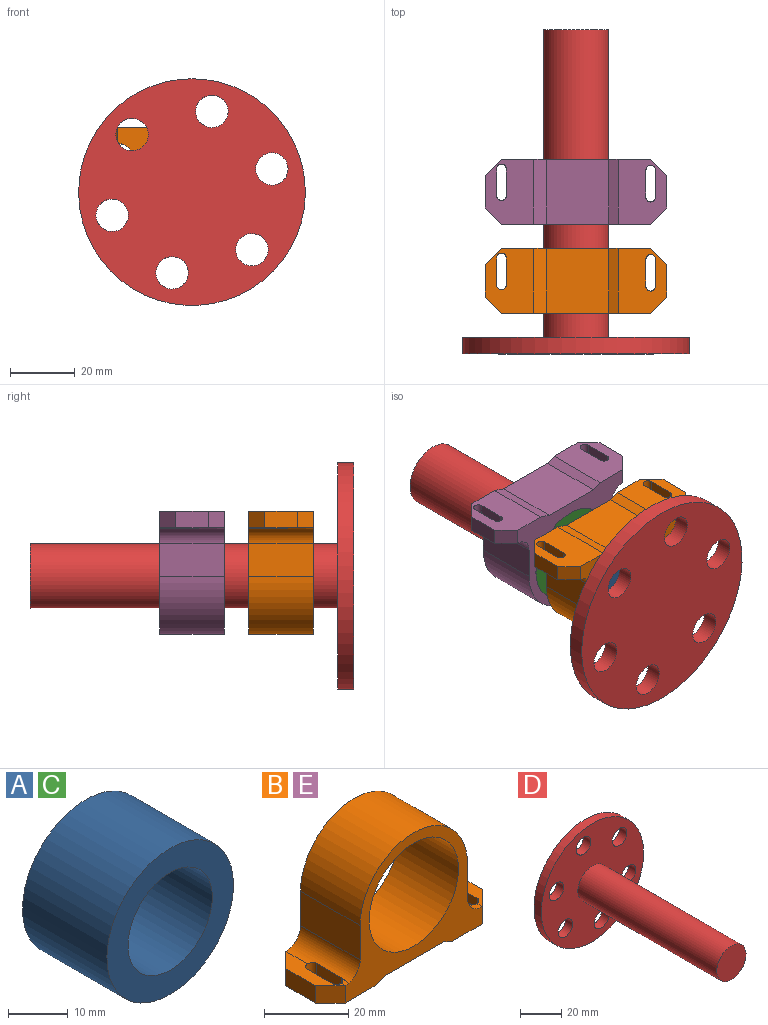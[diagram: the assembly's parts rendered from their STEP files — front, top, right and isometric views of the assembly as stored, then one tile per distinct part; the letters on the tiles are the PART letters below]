
ASSEMBLY  parts=5 mates=5
PART A: 4 faces, bbox 30x20x30 mm
  f0: cylinder r=10mm len=20mm, axis (0,1,0), area 1256.6mm2, adj f2,f3
  f1: cylinder r=15mm len=30mm, axis (0,1,0), area 1885mm2, adj f2,f3
  f2: plane 30x30mm, normal (0,-1,0), area 392.7mm2, adj f0,f1
  f3: plane 30x30mm, normal (0,1,0), area 392.7mm2, adj f0,f1
PART B: 33 faces, bbox 56x20x38 mm
  f0: plane 46x38mm, normal (0,-1,0), area 554.8mm2, adj f1,f2,f3,f6,f7,f8,f9,f10
  f1: plane 20x10.21mm, normal (1,0,0), area 202mm2, adj f0,f2,f13,f27,f28,f29,f30,f31
  f2: cylinder r=18mm len=36mm, axis (0,1,0), area 1131mm2, adj f0,f1,f3,f13
  f3: plane 20x10mm, normal (-1,0,0), area 200mm2, adj f0,f2,f13,f32
  f4: plane 20x5mm, normal (0,0,1), area 59.1mm2, adj f5,f20,f21,f22,f23,f24,f32
  f5: plane 10x5mm, normal (-1,0,0), area 50mm2, adj f4,f6,f23,f24
  f6: plane 20x15mm, normal (0,0,-1), area 243.1mm2, adj f0,f5,f7,f13,f19,f20,f21,f22
  f7: plane 20x3.8mm, normal (0.31,0,-0.95), area 80mm2, adj f0,f6,f8,f13
  f8: plane 20x19.25mm, normal (0,0,-1), area 385mm2, adj f0,f7,f9,f13
  f9: plane 20x2.95mm, normal (-0.39,0,-0.92), area 63.9mm2, adj f0,f8,f10,f13
  f10: plane 20x15mm, normal (0,0,-1), area 242.9mm2, adj f0,f9,f11,f13,f15,f16,f17,f18
  f11: plane 10x5mm, normal (1,0,0), area 50mm2, adj f10,f12,f25,f26
  f12: plane 20x5mm, normal (0,0,1), area 58.2mm2, adj f11,f15,f17,f18,f25,f26,f27,f31
  f13: plane 46x38mm, normal (0,1,0), area 554.8mm2, adj f1,f2,f3,f6,f7,f8,f9,f10
  f14: cylinder r=15mm len=30mm, axis (0,1,0), area 1885mm2, adj f0,f13
  f15: cylinder r=1.5mm len=5mm, axis (0,0,1), area 23.6mm2, adj f10,f12,f16,f18,f28
  f16: plane 8.33x5mm, normal (1,0,0), area 41.7mm2, adj f10,f15,f17,f29
  f17: cylinder r=1.5mm len=5mm, axis (0,0,1), area 23.6mm2, adj f10,f12,f16,f18,f30
  f18: plane 8.33x5mm, normal (-1,0,0), area 41.7mm2, adj f10,f12,f15,f17
  f19: plane 8.27x5.23mm, normal (-1,0,0), area 43.2mm2, adj f6,f20,f22,f32
  f20: cylinder r=1.5mm len=5.23mm, axis (0,0,1), area 23.8mm2, adj f4,f6,f19,f21,f32
  f21: plane 8.27x5mm, normal (1,0,0), area 41.3mm2, adj f4,f6,f20,f22
  f22: cylinder r=1.5mm len=5.23mm, axis (0,0,1), area 23.8mm2, adj f4,f6,f19,f21,f32
  f23: plane 5x5mm, normal (-0.71,-0.71,0), area 35.4mm2, adj f0,f4,f5,f6
  f24: plane 5x5mm, normal (-0.71,0.71,0), area 35.4mm2, adj f4,f5,f6,f13
  f25: plane 5x5mm, normal (0.71,0.71,0), area 35.4mm2, adj f10,f11,f12,f13
  f26: plane 5x5mm, normal (0.71,-0.71,0), area 35.4mm2, adj f0,f10,f11,f12
  f27: cylinder r=5mm len=6.85mm, axis (0,-1,0), area 53.8mm2, adj f1,f12,f13,f28
  f28: bspline ~5.03x5.01mm, area 10.3mm2, adj f1,f15,f27,f29
  f29: cylinder r=5mm len=8.33mm, axis (0,-1,0), area 53.3mm2, adj f1,f16,f28,f30
  f30: bspline ~5.02x5.01mm, area 10.2mm2, adj f1,f17,f29,f31
  f31: cylinder r=5mm len=5mm, axis (0,-1,0), area 14.3mm2, adj f0,f1,f12,f30
  f32: cylinder r=5mm len=20mm, axis (0,-1,0), area 142.2mm2, adj f0,f3,f4,f13,f19,f20,f22
PART C: same geometry as A
PART D: 11 faces, bbox 70x100x70 mm
  f0: cylinder r=10mm len=95mm, axis (0,1,0), area 5969mm2, adj f1,f3
  f1: plane 20x20mm, normal (0,-1,0), area 314.2mm2, adj f0
  f2: cylinder r=35mm len=70mm, axis (0,1,0), area 1099.6mm2, adj f3,f4
  f3: plane 70x70mm, normal (0,-1,0), area 3063.1mm2, adj f0,f2,f5,f6,f7,f8,f9,f10
  f4: plane 70x70mm, normal (0,1,0), area 3377.2mm2, adj f2,f5,f6,f7,f8,f9,f10
  f5: cylinder r=5mm len=10mm, axis (0,1,0), area 157.1mm2, adj f3,f4
  f6: cylinder r=5mm len=10mm, axis (0,1,0), area 157.1mm2, adj f3,f4
  f7: cylinder r=5mm len=10mm, axis (0,1,0), area 157.1mm2, adj f3,f4
  f8: cylinder r=5mm len=10mm, axis (0,1,0), area 157.1mm2, adj f3,f4
  f9: cylinder r=5mm len=10mm, axis (0,1,0), area 157.1mm2, adj f3,f4
  f10: cylinder r=5mm len=10mm, axis (0,1,0), area 157.1mm2, adj f3,f4
PART E: same geometry as B
PLACE A t=(-9.99,40.2,-23.55)mm
PLACE B rot(axis=(1,0,0),180deg) t=(-9.99,20.2,-23.55)mm fixed
PLACE C t=(-9.99,67.7,-23.55)mm
PLACE D rot(axis=(1,0,0),180deg) t=(-9.99,7.7,-23.55)mm
PLACE E rot(axis=(1,0,0),180deg) t=(-9.99,47.7,-23.55)mm
MATE fastened B.f14 <-> A.f1  axis (0,-1,0) through (-9.99,20.2,-23.55)mm
MATE fastened E.f14 <-> C.f1  axis (0,-1,0) through (-9.99,47.7,-23.55)mm
MATE revolute D.f0 <-> A.f0  axis (0,-1,0) through (-9.99,60.2,-23.55)mm
MATE revolute C.f0 <-> D.f0  axis (0,1,0) through (-9.99,67.7,-23.55)mm
MATE fastened C.f0 <-> E.f2  axis (0,1,0) through (-9.99,67.7,-23.55)mm
